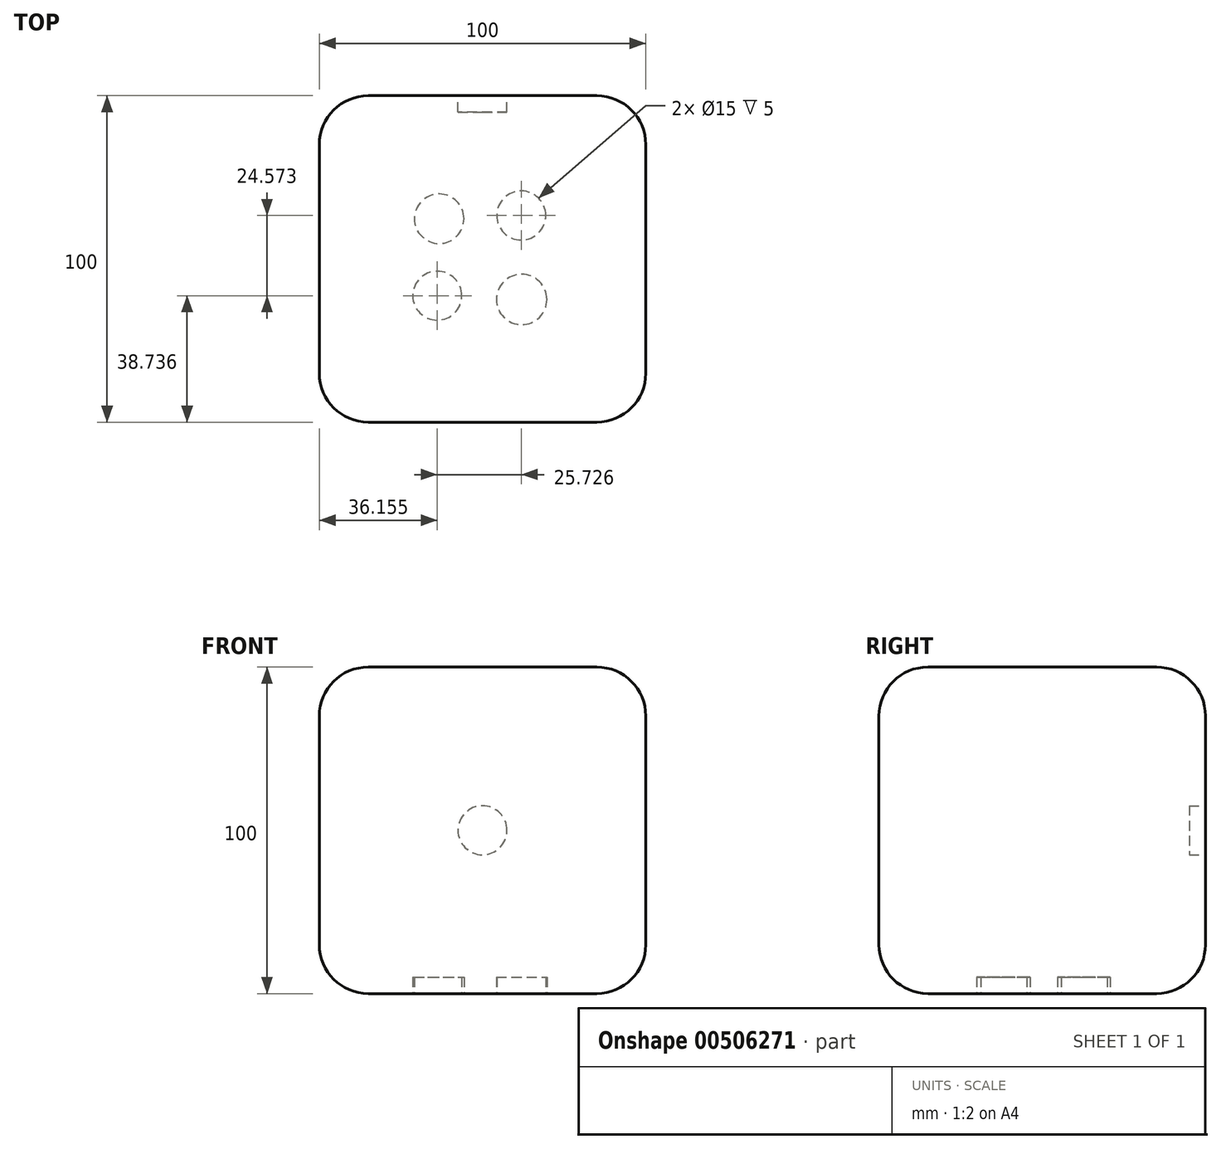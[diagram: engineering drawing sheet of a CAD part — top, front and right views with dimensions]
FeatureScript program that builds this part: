
annotation { "Feature Type Name" : "Feature", "Feature Type Description" : "" }
export const myFeature = defineFeature(function(context is Context, id is Id, definition is map)
    precondition{}
    {
        {
            var Q0;
            Q0=qCreatedBy(makeId("Top.planeOp"),FACE);
            var sketch = newSketch(context, id + "F0", { "sketchPlane" : qUnion([Q0])});
            skLineSegment(sketch, "E0.bottom", {"start": v(-47.54, 50.28) * mm, "end": v(52.46, 50.28) * mm});
            skLineSegment(sketch, "E0.top", {"start": v(-47.54, -49.72) * mm, "end": v(52.46, -49.72) * mm});
            skLineSegment(sketch, "E0.left", {"start": v(-47.54, 50.28) * mm, "end": v(-47.54, -49.72) * mm});
            skLineSegment(sketch, "E0.right", {"start": v(52.46, 50.28) * mm, "end": v(52.46, -49.72) * mm});
            skSolve(sketch);
        }
        {
            var Q0;
            Q0 = qSketchRegion(id + "F0", true);
            extrude(context, id + "F1", {"entities" : qUnion([Q0]), "depth" : 100 * mm});
        }
        {
            var Q0;
            Q0=makeQuery(id+"F1.opExtrude","CAP_EDGE",EDGE,{"disambiguationData":[OSD([sQuery(id+"F0.wireOp",EDGE,"E0.bottom")])],"isStart":true});
            var Q1;
            Q1=makeQuery(id+"F1.opExtrude","SWEPT_EDGE",EDGE,{"disambiguationData":[OSD([sQuery(id+"F0.wireOp",EDGE,"E0.bottom"),sQuery(id+"F0.wireOp",EDGE,"E0.left")])]});
            var Q2;
            Q2=makeQuery(id+"F1.opExtrude","CAP_EDGE",EDGE,{"disambiguationData":[OSD([sQuery(id+"F0.wireOp",EDGE,"E0.bottom")])],"isStart":false});
            var Q3;
            Q3=makeQuery(id+"F1.opExtrude","SWEPT_EDGE",EDGE,{"disambiguationData":[OSD([sQuery(id+"F0.wireOp",EDGE,"E0.bottom"),sQuery(id+"F0.wireOp",EDGE,"E0.right")])]});
            var Q4;
            Q4=makeQuery(id+"F1.opExtrude","CAP_FACE",FACE,{"disambiguationData":[OSD([sQuery(id+"F0.wireOp",EDGE,"E0.bottom"),sQuery(id+"F0.wireOp",EDGE,"E0.top"),sQuery(id+"F0.wireOp",EDGE,"E0.left"),sQuery(id+"F0.wireOp",EDGE,"E0.right")])],"isStart":true});
            var Q5;
            Q5=makeQuery(id+"F1.opExtrude","SWEPT_FACE",FACE,{"disambiguationData":[OSD([sQuery(id+"F0.wireOp",EDGE,"E0.left")])]});
            var Q6;
            Q6=makeQuery(id+"F1.opExtrude","CAP_EDGE",EDGE,{"disambiguationData":[OSD([sQuery(id+"F0.wireOp",EDGE,"E0.right")])],"isStart":false});
            var Q7;
            Q7=makeQuery(id+"F1.opExtrude","SWEPT_EDGE",EDGE,{"disambiguationData":[OSD([sQuery(id+"F0.wireOp",EDGE,"E0.top"),sQuery(id+"F0.wireOp",EDGE,"E0.right")])]});
            var Q8;
            Q8=makeQuery(id+"F1.opExtrude","CAP_EDGE",EDGE,{"disambiguationData":[OSD([sQuery(id+"F0.wireOp",EDGE,"E0.top")])],"isStart":false});
            fillet(context, id + "F2", {"entities" : qUnion([Q0, Q1, Q2, Q3, Q4, Q5, Q6, Q7, Q8]), "radius" : 15 * mm, "tangentPropagation" : true, "allowEdgeOverflow" : false});
        }
        {
            var Q0;
            Q0=makeQuery(id+"F1.opExtrude","SWEPT_FACE",FACE,{"disambiguationData":[OSD([sQuery(id+"F0.wireOp",EDGE,"E0.bottom")])]});
            var sketch = newSketch(context, id + "F3", { "sketchPlane" : qUnion([Q0])});
            skCircle(sketch, "E1", {"center": v(-2.46, 50) * mm, "radius": 7.5 * mm});
            skSolve(sketch);
        }
        {
            var Q0;
            Q0 = qSketchRegion(id + "F3", true);
            extrude(context, id + "F4", {"entities" : qUnion([Q0]), "operationType" : NewBodyOperationType.REMOVE, "oppositeDirection" : true, "depth" : 5 * mm, "offsetDistance" : 25 * mm});
        }
        {
            var Q0;
            Q0=makeQuery(id+"F1.opExtrude","CAP_FACE",FACE,{"disambiguationData":[OSD([sQuery(id+"F0.wireOp",EDGE,"E0.bottom"),sQuery(id+"F0.wireOp",EDGE,"E0.top"),sQuery(id+"F0.wireOp",EDGE,"E0.left"),sQuery(id+"F0.wireOp",EDGE,"E0.right")])],"isStart":true});
            var sketch = newSketch(context, id + "F5", { "sketchPlane" : qUnion([Q0])});
            skCircle(sketch, "E2", {"center": v(14.34, -13.59) * mm, "radius": 7.5 * mm});
            skCircle(sketch, "E3", {"center": v(-10.8, -12.57) * mm, "radius": 7.59 * mm});
            skCircle(sketch, "E4", {"center": v(14.47, 12.13) * mm, "radius": 7.71 * mm});
            skCircle(sketch, "E5", {"center": v(-11.39, 10.98) * mm, "radius": 7.5 * mm});
            skSolve(sketch);
        }
        {
            var Q0;
            Q0 = qSketchRegion(id + "F5", true);
            extrude(context, id + "F6", {"entities" : qUnion([Q0]), "operationType" : NewBodyOperationType.REMOVE, "oppositeDirection" : true, "depth" : 5 * mm, "offsetDistance" : 25 * mm});
        }
    });
